# Revit family: Handshower-American_Standard-Spectra_Plus_Handheld-9035.154
name_source: partatom
category: Plumbing Fixtures
units: mm (PartAtom-declared; Revit-internal decimal feet)

## family parameters
Always vertical = No
Cut with Voids When Loaded = No
OmniClass Number = 23.45.05.14.17
OmniClass Title = Showers
Part Type = Normal
Room Calculation Point = No
Round Connector Dimension = Use Diameter
Shared = Yes
Work Plane-Based = Yes

## types (3) — shared parameters
1660.400 - Vacuum Breaker = No
8888.035 - 59" Metal Shower Hose = No
8888.036 - Fixed Wall Bracket = No
8888.037 - Wall Supply = No
8888.038 Wall Supply Bracket = No
8888.053 - 79" Metal Shower Hose = No
8888.068 - Round Wall Supply = No
8888.069 - Square Wall Supply = No
8888.096 - Shower Arm Bracket = No
Assembly Code = D2010710
CW Connection = Yes
CWFU = 3
Default Elevation = 0"
Description = Spectra® Handheld 2.5 gpm/9.5 L/min 5-Inch 4-Function Hand Shower
Flow Rate = 2.5 gpm/9.5 L/min
HW Connection = Yes
HWFU = 3
Height = 10 1/16"
IAPMO Compliance = ASME A112.18.1 and CSA B125.1
Length = 4 15/16"
Manufacturer = American Standard
Price = Prices may vary. Please consult Manufacturer Representative for most up-to-date price list.
Product Documentation Link = https://americanstandard.box.com
Revised Date = 08/04/2022
Tempered Water Connection Diameter = 1/2"
Tempered Water Connection Radius = 1/4"
URL = https://www.americanstandard-us.com
Vent Connection = No
WFU = 4
Warranty Information = One Year General Product Warranty
Waste Connection = No
Width = 1 3/4"

## per-type parameters (varying)
| type | Finish | Material | Product Page URL |
| 9035154.002 | Brass-American Standard-002-Polished Chrome | Brass-American Standard-002-Polished Chrome | https://americanstandard-us.com |
| 9035154.295 | Brass-American Standard-295-Brushed Nickel | Brass-American Standard-295-Brushed Nickel | https://americanstandard-us.com |
| 9035154.278 | Brass-American Standard-278-Legacy Bronze | Brass-American Standard-278-Legacy Bronze | https://americahttps: |

note: column(s) folded — value = type name in every type: Model

## geometry (parser evidence)
native form markers: Sweep x2
no freeform markers — native parametric forms only
